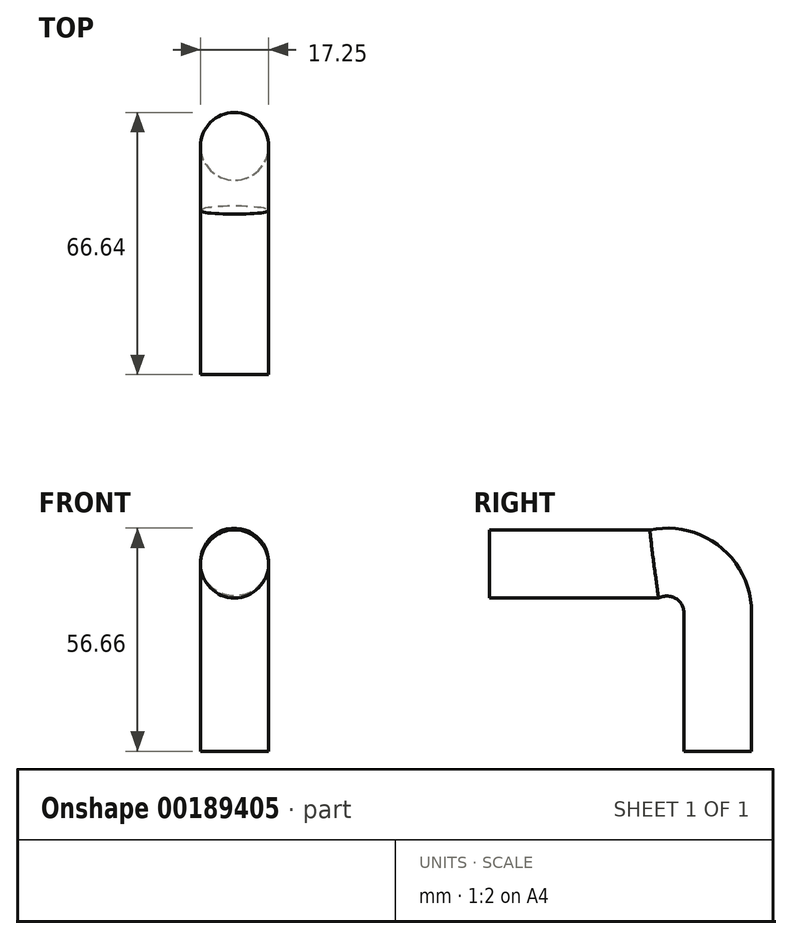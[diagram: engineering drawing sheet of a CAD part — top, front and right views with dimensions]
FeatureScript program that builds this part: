
annotation { "Feature Type Name" : "Feature", "Feature Type Description" : "" }
export const myFeature = defineFeature(function(context is Context, id is Id, definition is map)
    precondition{}
    {
        {
            var Q0;
            Q0=qCreatedBy(makeId("Top.planeOp"),FACE);
            var sketch = newSketch(context, id + "F0", { "sketchPlane" : qUnion([Q0])});
            skCircle(sketch, "E0", {"center": v(-34.62, 14.82) * mm, "radius": 8.63 * mm});
            skSolve(sketch);
        }
        {
            var Q0;
            Q0=qCreatedBy(makeId("Right.planeOp"),FACE);
            var sketch = newSketch(context, id + "F1", { "sketchPlane" : qUnion([Q0])});
            skLineSegment(sketch, "E1", {"start": v(14.82, 0) * mm, "end": v(14.82, 35.24) * mm});
            skArc(sketch, "E2", {"start": v(14.82, 35.24) * mm, "mid": v(9.76, 45.43) * mm, "end": v(-1.4, 47.57) * mm});
            skLineSegment(sketch, "E3", {"start": v(-1.4, 47.57) * mm, "end": v(-43.2, 47.57) * mm});
            skSolve(sketch);
        }
        {
            var Q0;
            Q0 = qSketchRegion(id + "F0", true);
            var Q1;
            Q1 = qConstructionFilter(qBodyType(qCreatedBy(id + "F1" ,EDGE), BodyType.WIRE), ConstructionObject.NO);
            sweep(context, id + "F2", {"profiles" : qUnion([Q0]), "path" : qUnion([Q1])});
        }
    });
